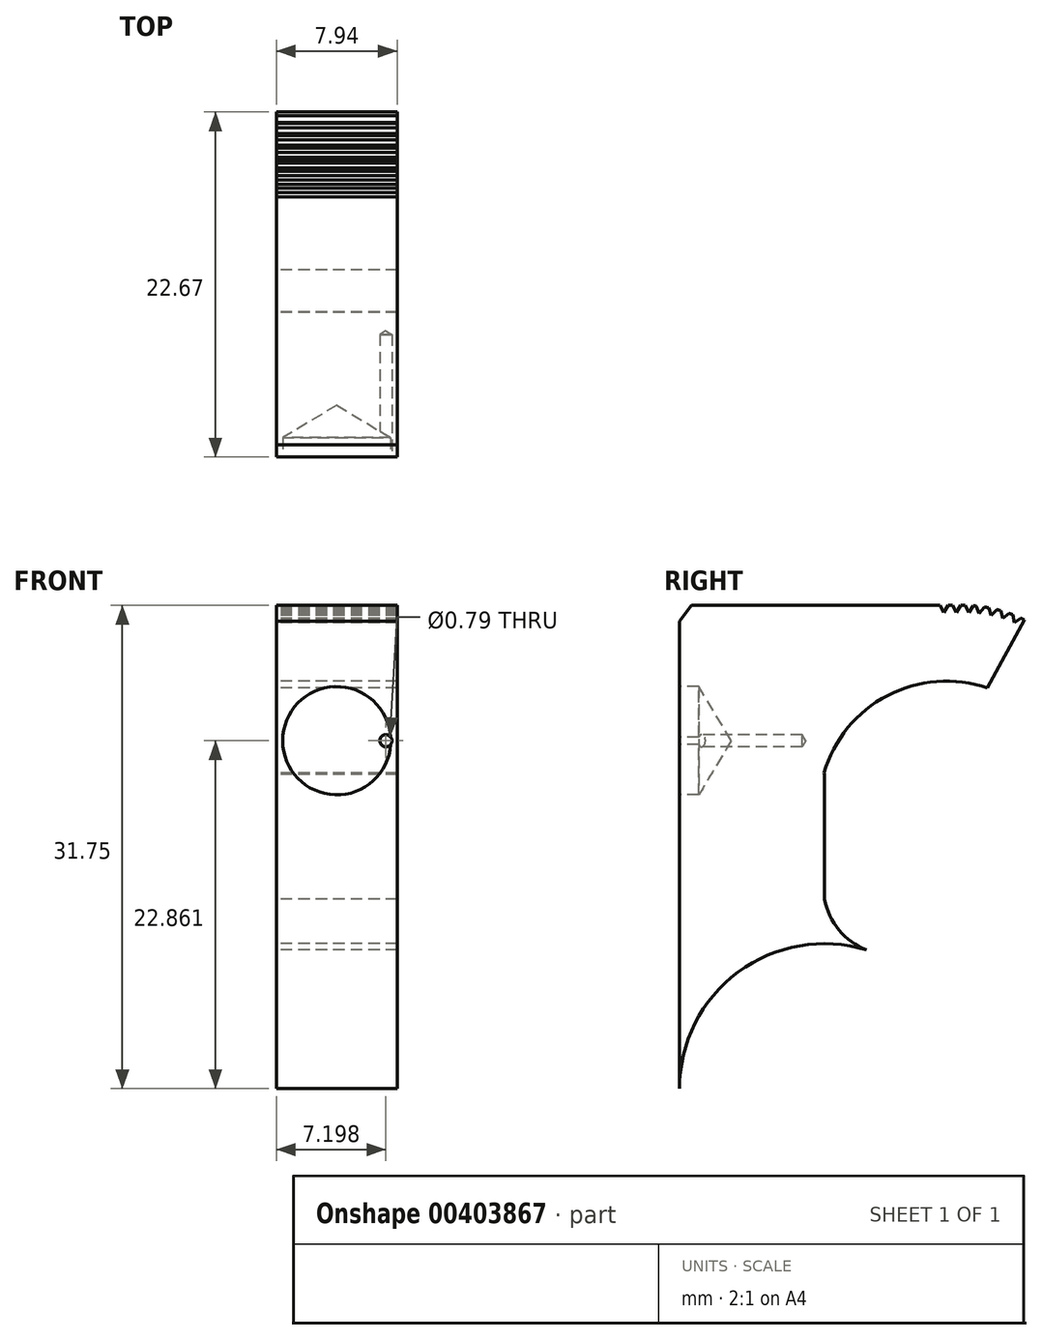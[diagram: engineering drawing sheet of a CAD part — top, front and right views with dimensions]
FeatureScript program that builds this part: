
annotation { "Feature Type Name" : "Feature", "Feature Type Description" : "" }
export const myFeature = defineFeature(function(context is Context, id is Id, definition is map)
    precondition{}
    {
        {
            var Q0;
            Q0=qCreatedBy(makeId("Right.planeOp"),FACE);
            var sketch = newSketch(context, id + "F0", { "sketchPlane" : qUnion([Q0])});
            skArc(sketch, "E0", {"start": v(-3.83, -19.2) * mm, "mid": v(-12.53, -20.38) * mm, "end": v(-16.58, -28.17) * mm});
            skLineSegment(sketch, "E1", {"start": v(-16.58, -28.17) * mm, "end": v(-16.58, 2.54) * mm});
            skLineSegment(sketch, "E2", {"start": v(-7.04, -15.73) * mm, "end": v(-7.04, -7.53) * mm});
            skLineSegment(sketch, "E3", {"start": v(-15.8, 3.58) * mm, "end": v(0.52, 3.58) * mm});
            skArc(sketch, "E4", {"start": v(3.66, -1.85) * mm, "mid": v(-2.9, -2.34) * mm, "end": v(-7.08, -7.43) * mm});
            skLineSegment(sketch, "E5", {"start": v(6.09, 2.63) * mm, "end": v(3.66, -1.85) * mm});
            skLineSegment(sketch, "E6", {"start": v(-7.08, -7.43) * mm, "end": v(-7.04, -7.53) * mm});
            skArc(sketch, "E7", {"start": v(-7.04, -15.73) * mm, "mid": v(-5.94, -17.93) * mm, "end": v(-3.83, -19.2) * mm});
            skLineSegment(sketch, "E8", {"start": v(-15.8, 3.58) * mm, "end": v(-16.58, 2.54) * mm});
            skLineSegment(sketch, "E9", {"start": v(2.18, 3.58) * mm, "end": v(2.43, 3.12) * mm});
            skLineSegment(sketch, "E10", {"start": v(2.43, 3.12) * mm, "end": v(2.74, 3.56) * mm});
            skArc(sketch, "E11", {"start": v(2.74, 3.56) * mm, "mid": v(2.82, 3.55) * mm, "end": v(2.9, 3.54) * mm});
            skLineSegment(sketch, "E12", {"start": v(2.9, 3.54) * mm, "end": v(3.11, 3.07) * mm});
            skLineSegment(sketch, "E13", {"start": v(3.11, 3.07) * mm, "end": v(3.45, 3.48) * mm});
            skArc(sketch, "E14.trimOffspring", {"start": v(3.45, 3.48) * mm, "mid": v(3.59, 3.45) * mm, "end": v(3.73, 3.43) * mm});
            skLineSegment(sketch, "E15", {"start": v(3.73, 3.43) * mm, "end": v(3.9, 2.93) * mm});
            skLineSegment(sketch, "E16", {"start": v(3.9, 2.93) * mm, "end": v(4.27, 3.3) * mm});
            skArc(sketch, "E17.trimOffspring", {"start": v(4.27, 3.3) * mm, "mid": v(4.4, 3.27) * mm, "end": v(4.54, 3.23) * mm});
            skLineSegment(sketch, "E18", {"start": v(4.54, 3.23) * mm, "end": v(4.68, 2.72) * mm});
            skLineSegment(sketch, "E19", {"start": v(4.68, 2.72) * mm, "end": v(5.07, 3.07) * mm});
            skArc(sketch, "E20.trimOffspring", {"start": v(5.07, 3.07) * mm, "mid": v(5.2, 3.02) * mm, "end": v(5.33, 2.97) * mm});
            skLineSegment(sketch, "E21", {"start": v(5.33, 2.97) * mm, "end": v(5.41, 2.44) * mm});
            skLineSegment(sketch, "E22", {"start": v(5.41, 2.44) * mm, "end": v(5.84, 2.75) * mm});
            skArc(sketch, "E23.trimOffspring", {"start": v(5.84, 2.75) * mm, "mid": v(5.97, 2.7) * mm, "end": v(6.09, 2.63) * mm});
            skLineSegment(sketch, "E24", {"start": v(1.35, 3.58) * mm, "end": v(1.63, 3.13) * mm});
            skLineSegment(sketch, "E25", {"start": v(1.63, 3.13) * mm, "end": v(1.9, 3.58) * mm});
            skLineSegment(sketch, "E26.trimOffspring", {"start": v(1.9, 3.58) * mm, "end": v(2.18, 3.58) * mm});
            skLineSegment(sketch, "E27", {"start": v(0.52, 3.58) * mm, "end": v(0.8, 3.13) * mm});
            skLineSegment(sketch, "E28", {"start": v(0.8, 3.13) * mm, "end": v(1.07, 3.58) * mm});
            skLineSegment(sketch, "E29.trimOffspring", {"start": v(1.07, 3.58) * mm, "end": v(1.35, 3.58) * mm});
            skSolve(sketch);
        }
        {
            var Q0;
            {var subQ1=sQuery(id+"F0.wireOp",EDGE,"E1");Q0=makeQuery(id+"F0.imprint","IMPRINT",FACE,{"disambiguationData":[TD([[makeQuery(id+"F0.imprint","IMPRINT",EDGE,{"derivedFrom":subQ1}),-1.0]])]});}
            extrude(context, id + "F1", {"entities" : qUnion([Q0]), "endBound" : BoundingType.SYMMETRIC, "depth" : 7.94 * mm});
        }
        {
            var Q0;
            Q0=makeQuery(id+"F1.opExtrude","SWEPT_FACE",FACE,{"disambiguationData":[OSD([sQuery(id+"F0.wireOp",EDGE,"E1")])]});
            var sketch = newSketch(context, id + "F2", { "sketchPlane" : qUnion([Q0])});
            skCircle(sketch, "E30", {"center": v(3.23, -5.3) * mm, "radius": 0.4 * mm});
            skCircle(sketch, "E31", {"center": v(0, -5.3) * mm, "radius": 3.56 * mm});
            skSolve(sketch);
        }
        {
            var Q0;
            Q0=sQuery(id+"F2.wireOp",VERTEX,"E31.center");
            var Q1;
            Q1=makeQuery(id+"F1.opExtrude","SWEPT_BODY",BODY,{"disambiguationData":[OSD([sQuery(id+"F0.wireOp",EDGE,"E0"),sQuery(id+"F0.wireOp",EDGE,"E1"),sQuery(id+"F0.wireOp",EDGE,"E2"),sQuery(id+"F0.wireOp",EDGE,"E3"),sQuery(id+"F0.wireOp",EDGE,"E4"),sQuery(id+"F0.wireOp",EDGE,"E5"),sQuery(id+"F0.wireOp",EDGE,"E6"),sQuery(id+"F0.wireOp",EDGE,"E7"),sQuery(id+"F0.wireOp",EDGE,"E8"),sQuery(id+"F0.wireOp",EDGE,"E9"),sQuery(id+"F0.wireOp",EDGE,"E10"),sQuery(id+"F0.wireOp",EDGE,"E11"),sQuery(id+"F0.wireOp",EDGE,"E12"),sQuery(id+"F0.wireOp",EDGE,"E13"),sQuery(id+"F0.wireOp",EDGE,"E14.trimOffspring"),sQuery(id+"F0.wireOp",EDGE,"E15"),sQuery(id+"F0.wireOp",EDGE,"E16"),sQuery(id+"F0.wireOp",EDGE,"E17.trimOffspring"),sQuery(id+"F0.wireOp",EDGE,"E18"),sQuery(id+"F0.wireOp",EDGE,"E19"),sQuery(id+"F0.wireOp",EDGE,"E20.trimOffspring"),sQuery(id+"F0.wireOp",EDGE,"E21"),sQuery(id+"F0.wireOp",EDGE,"E22"),sQuery(id+"F0.wireOp",EDGE,"E23.trimOffspring"),sQuery(id+"F0.wireOp",EDGE,"E24"),sQuery(id+"F0.wireOp",EDGE,"E25"),sQuery(id+"F0.wireOp",EDGE,"E26.trimOffspring"),sQuery(id+"F0.wireOp",EDGE,"E27"),sQuery(id+"F0.wireOp",EDGE,"E28"),sQuery(id+"F0.wireOp",EDGE,"E29.trimOffspring")])]});
            hole(context, id + "F3", {"style" : HoleStyle.SIMPLE, "endStyle" : HoleEndStyle.BLIND, "holeDiameter" : 7.11 * mm, "holeDepth" : 1.27 * mm, "isTappedThrough" : true, "tappedDepth" : 12.7 * mm, "tapClearance" : 3, "locations" : qUnion([Q0]), "scope" : qUnion([Q1])});
        }
        {
            var Q0;
            Q0=sQuery(id+"F2.wireOp",VERTEX,"E30.center");
            var Q1;
            Q1=makeQuery(id+"F1.opExtrude","SWEPT_BODY",BODY,{"disambiguationData":[OSD([sQuery(id+"F0.wireOp",EDGE,"E0"),sQuery(id+"F0.wireOp",EDGE,"E1"),sQuery(id+"F0.wireOp",EDGE,"E2"),sQuery(id+"F0.wireOp",EDGE,"E3"),sQuery(id+"F0.wireOp",EDGE,"E4"),sQuery(id+"F0.wireOp",EDGE,"E5"),sQuery(id+"F0.wireOp",EDGE,"E6"),sQuery(id+"F0.wireOp",EDGE,"E7"),sQuery(id+"F0.wireOp",EDGE,"E8"),sQuery(id+"F0.wireOp",EDGE,"E9"),sQuery(id+"F0.wireOp",EDGE,"E10"),sQuery(id+"F0.wireOp",EDGE,"E11"),sQuery(id+"F0.wireOp",EDGE,"E12"),sQuery(id+"F0.wireOp",EDGE,"E13"),sQuery(id+"F0.wireOp",EDGE,"E14.trimOffspring"),sQuery(id+"F0.wireOp",EDGE,"E15"),sQuery(id+"F0.wireOp",EDGE,"E16"),sQuery(id+"F0.wireOp",EDGE,"E17.trimOffspring"),sQuery(id+"F0.wireOp",EDGE,"E18"),sQuery(id+"F0.wireOp",EDGE,"E19"),sQuery(id+"F0.wireOp",EDGE,"E20.trimOffspring"),sQuery(id+"F0.wireOp",EDGE,"E21"),sQuery(id+"F0.wireOp",EDGE,"E22"),sQuery(id+"F0.wireOp",EDGE,"E23.trimOffspring"),sQuery(id+"F0.wireOp",EDGE,"E24"),sQuery(id+"F0.wireOp",EDGE,"E25"),sQuery(id+"F0.wireOp",EDGE,"E26.trimOffspring"),sQuery(id+"F0.wireOp",EDGE,"E27"),sQuery(id+"F0.wireOp",EDGE,"E28"),sQuery(id+"F0.wireOp",EDGE,"E29.trimOffspring")])]});
            hole(context, id + "F4", {"style" : HoleStyle.SIMPLE, "endStyle" : HoleEndStyle.BLIND, "holeDiameter" : 0.8 * mm, "holeDepth" : 6.35 * mm, "isTappedThrough" : true, "tappedDepth" : 12.7 * mm, "tapClearance" : 3, "locations" : qUnion([Q0]), "scope" : qUnion([Q1])});
        }
    });
